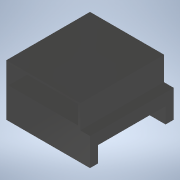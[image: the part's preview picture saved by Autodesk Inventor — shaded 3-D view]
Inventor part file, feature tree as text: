
AUTODESK INVENTOR PART (.ipt)
format: ipt  version: 2021.3 (Build 253353010, 353A)  size: 147,456 bytes
history: native  units: mm
features: extrude x4, sketch x4, projected_geometry x1
ambient origin geometry x8: Origin, YZ Plane, XZ Plane, XY Plane, X Axis, Y Axis, Z Axis, Center Point
bodies: Volumenkörper1 (feature_tree)
feature tree (9):
  extrude  "Extrusion1"  Depth=105.0mm
  extrude  "Extrusion2"  Depth=45.0mm
  extrude  "Extrusion3"  Depth=105.0mm
  extrude  "Extrusion4"  Depth=10.0mm
  sketch  "Skizze1"  dims[d0=105.0mm d1=105.0mm]
  sketch  "Skizze2"  dims[d2=93.0mm d3=45.0mm]
  sketch  "Skizze3"  dims[d4=0.0mm d5=105.0mm]
  sketch  "Skizze4"  dims[d6=10.0mm d7=10.0mm d8=20.0mm d9=0.0mm d10=15.0mm d11=0.0mm d12=3.0mm d13=3.0mm d14=23.0mm d15=0.0mm d16=0.0mm]
  projected_geometry  "Projizierte Kontur1"
